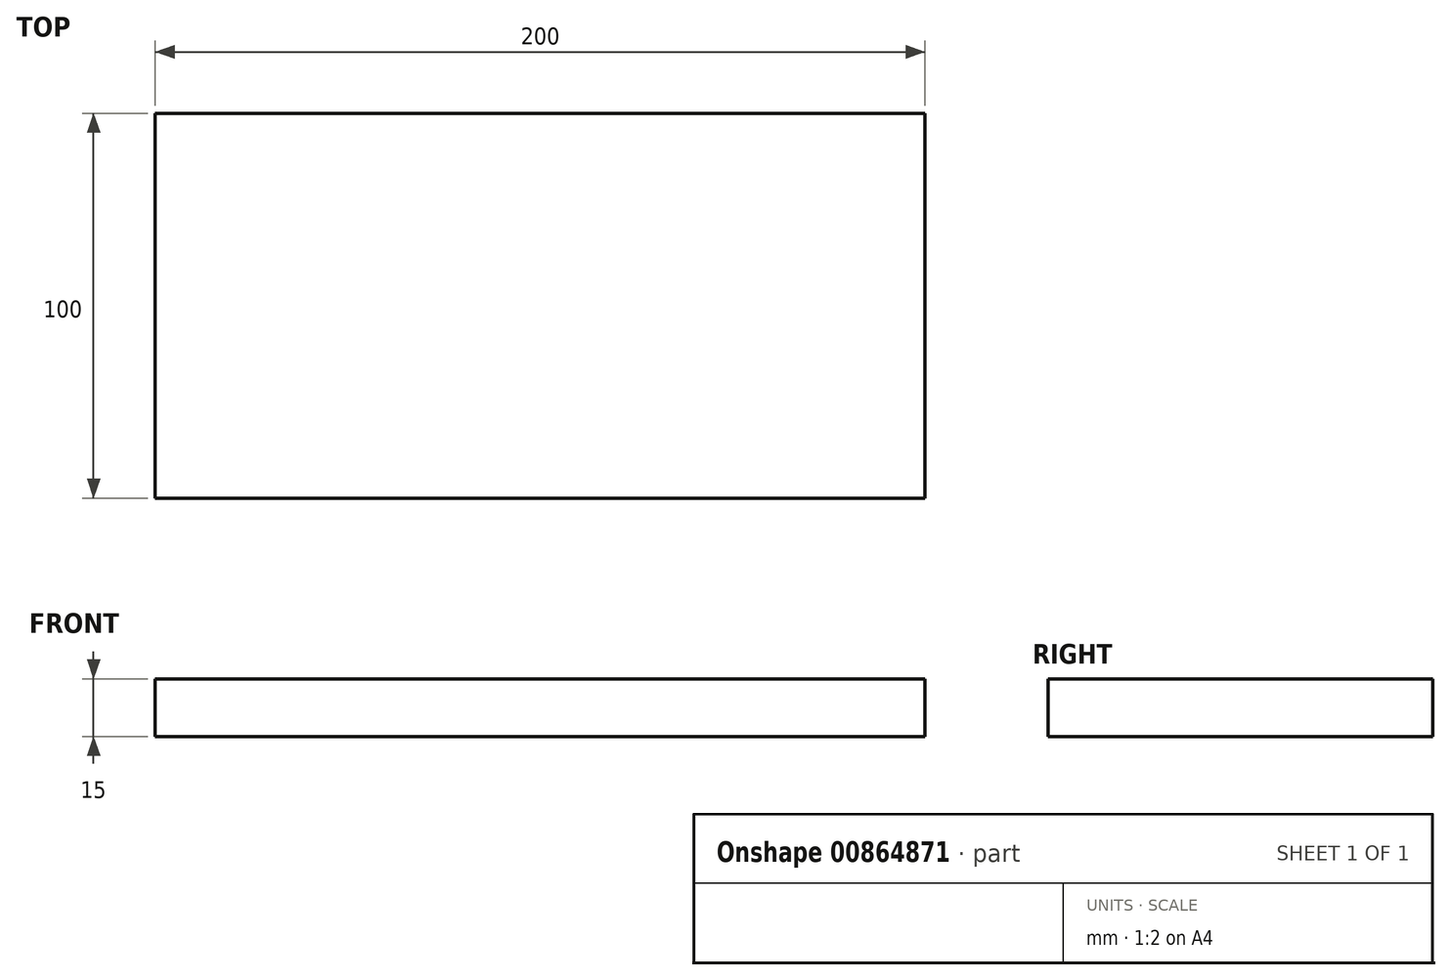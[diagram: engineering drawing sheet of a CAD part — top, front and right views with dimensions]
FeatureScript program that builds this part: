
annotation { "Feature Type Name" : "Feature", "Feature Type Description" : "" }
export const myFeature = defineFeature(function(context is Context, id is Id, definition is map)
    precondition{}
    {
        {
            var Q0;
            Q0=qCreatedBy(makeId("Top.planeOp"),FACE);
            var sketch = newSketch(context, id + "F0", { "sketchPlane" : qUnion([Q0])});
            skLineSegment(sketch, "E0.bottom", {"start": v(100, -50) * mm, "end": v(-100, -50) * mm});
            skLineSegment(sketch, "E0.top", {"start": v(100, 50) * mm, "end": v(-100, 50) * mm});
            skLineSegment(sketch, "E0.left", {"start": v(100, -50) * mm, "end": v(100, 50) * mm});
            skLineSegment(sketch, "E0.right", {"start": v(-100, -50) * mm, "end": v(-100, 50) * mm});
            skPoint(sketch, "E0.middle", {"position": v(0, 0) * mm});
            skSolve(sketch);
        }
        {
            var Q0;
            Q0=makeQuery(id+"F0.imprint","IMPRINT",FACE,{"disambiguationData":[TD([[makeQuery(id+"F0.imprint","IMPRINT",EDGE,{"derivedFrom":sQuery(id+"F0.wireOp",EDGE,"E0.bottom")}),-1.0]])]});
            extrude(context, id + "F1", {"entities" : qUnion([Q0]), "depth" : 15 * mm, "offsetDistance" : 25 * mm});
        }
    });
